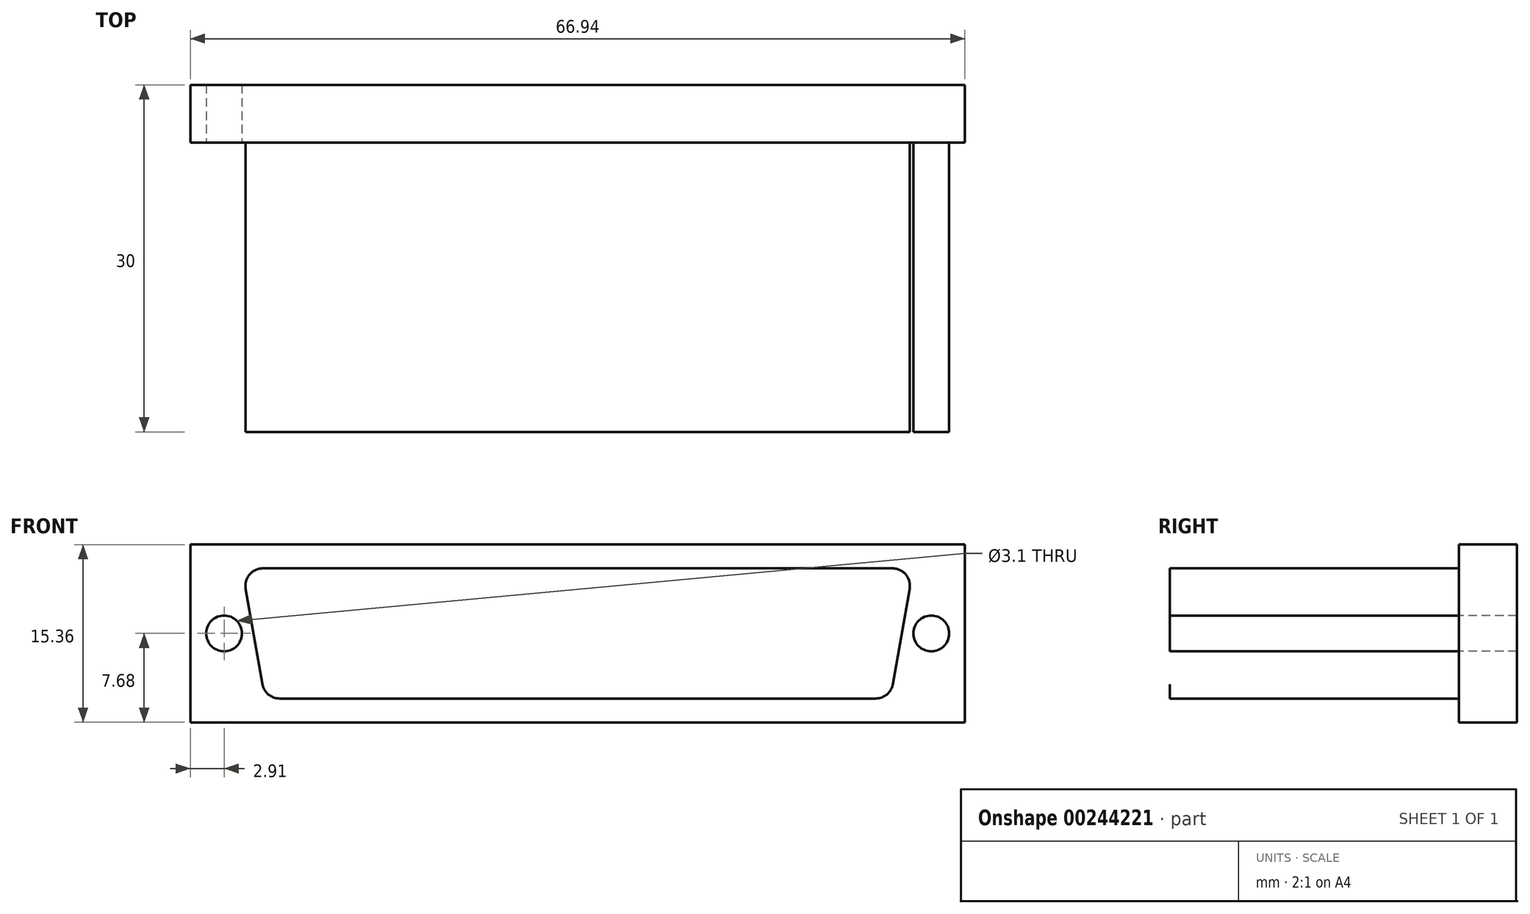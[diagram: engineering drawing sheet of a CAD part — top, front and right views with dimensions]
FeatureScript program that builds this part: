
annotation { "Feature Type Name" : "Feature", "Feature Type Description" : "" }
export const myFeature = defineFeature(function(context is Context, id is Id, definition is map)
    precondition{}
    {
        {
            var Q0;
            Q0=qCreatedBy(makeId("Front.planeOp"),FACE);
            var sketch = newSketch(context, id + "F0", { "sketchPlane" : qUnion([Q0])});
            skLineSegment(sketch, "E0.bottom", {"start": v(-33.47, 7.68) * mm, "end": v(33.47, 7.68) * mm});
            skLineSegment(sketch, "E0.top", {"start": v(-33.47, -7.68) * mm, "end": v(33.47, -7.68) * mm});
            skLineSegment(sketch, "E0.left", {"start": v(-33.47, 7.68) * mm, "end": v(-33.47, -7.68) * mm});
            skLineSegment(sketch, "E0.right", {"start": v(33.47, 7.68) * mm, "end": v(33.47, -7.68) * mm});
            skPoint(sketch, "E0.middle", {"position": v(0, 0) * mm});
            skCircle(sketch, "E1", {"center": v(30.56, 0) * mm, "radius": 1.55 * mm});
            skLineSegment(sketch, "E2", {"start": v(-33.47, 5.62) * mm, "end": v(33.47, 5.62) * mm, "construction": true});
            skLineSegment(sketch, "E3.MirrorCS", {"start": v(-33.47, -5.62) * mm, "end": v(33.47, -5.62) * mm, "construction": true});
            skCircle(sketch, "E4.MirrorC", {"center": v(-30.56, 0) * mm, "radius": 1.55 * mm});
            skLineSegment(sketch, "E5", {"start": v(28.69, 3.86) * mm, "end": v(27.23, -4.39) * mm});
            skLineSegment(sketch, "E6", {"start": v(29, 5.62) * mm, "end": v(29, -21.88) * mm, "construction": true});
            skLineSegment(sketch, "E7", {"start": v(0, 5.62) * mm, "end": v(27.21, 5.62) * mm});
            skLineSegment(sketch, "E8", {"start": v(0, -5.62) * mm, "end": v(25.76, -5.63) * mm});
            skPoint(sketch, "E9.visualSharp", {"position": v(29, 5.63) * mm});
            skArc(sketch, "E9.filletArc", {"start": v(28.69, 3.86) * mm, "mid": v(28.36, 5.09) * mm, "end": v(27.21, 5.62) * mm});
            skPoint(sketch, "E10.visualSharp", {"position": v(27.02, -5.63) * mm});
            skArc(sketch, "E10.filletArc", {"start": v(25.76, -5.63) * mm, "mid": v(26.72, -5.27) * mm, "end": v(27.23, -4.39) * mm});
            skLineSegment(sketch, "E11.MirrorCS", {"start": v(0, -5.62) * mm, "end": v(-25.76, -5.63) * mm});
            skLineSegment(sketch, "E12.MirrorCS", {"start": v(0, 5.62) * mm, "end": v(-27.21, 5.62) * mm});
            skLineSegment(sketch, "E13.MirrorCS", {"start": v(-28.69, 3.86) * mm, "end": v(-27.23, -4.39) * mm});
            skArc(sketch, "E14.MirrorCS", {"start": v(-28.69, 3.86) * mm, "mid": v(-28.36, 5.09) * mm, "end": v(-27.21, 5.62) * mm});
            skArc(sketch, "E15.MirrorCS", {"start": v(-25.76, -5.63) * mm, "mid": v(-26.72, -5.27) * mm, "end": v(-27.23, -4.39) * mm});
            skSolve(sketch);
        }
        {
            var Q0;
            Q0=makeQuery(id+"F0.imprint","IMPRINT",FACE,{"disambiguationData":[TD([[makeQuery(id+"F0.imprint","IMPRINT",EDGE,{"derivedFrom":sQuery(id+"F0.wireOp",EDGE,"E5")}),-1.0]])]});
            var Q1;
            Q1=makeQuery(id+"F0.imprint","IMPRINT",FACE,{"disambiguationData":[TD([[makeQuery(id+"F0.imprint","IMPRINT",EDGE,{"derivedFrom":sQuery(id+"F0.wireOp",EDGE,"E4.MirrorC")}),-1.0]])]});
            var Q2;
            Q2=makeQuery(id+"F0.imprint","IMPRINT",FACE,{"disambiguationData":[TD([[makeQuery(id+"F0.imprint","IMPRINT",EDGE,{"derivedFrom":sQuery(id+"F0.wireOp",EDGE,"E1")}),1.0]])]});
            extrude(context, id + "F1", {"entities" : qUnion([Q0, Q1, Q2]), "depth" : 25 * mm});
        }
        {
            var Q0;
            Q0=makeQuery(id+"F0.imprint","IMPRINT",FACE,{"disambiguationData":[TD([[makeQuery(id+"F0.imprint","IMPRINT",EDGE,{"derivedFrom":sQuery(id+"F0.wireOp",EDGE,"E0.bottom")}),-1.0]])]});
            var Q1;
            Q1=makeQuery(id+"F0.imprint","IMPRINT",FACE,{"disambiguationData":[TD([[makeQuery(id+"F0.imprint","IMPRINT",EDGE,{"derivedFrom":sQuery(id+"F0.wireOp",EDGE,"E5")}),-1.0]])]});
            var Q2;
            Q2=makeQuery(id+"F0.imprint","IMPRINT",FACE,{"disambiguationData":[TD([[makeQuery(id+"F0.imprint","IMPRINT",EDGE,{"derivedFrom":sQuery(id+"F0.wireOp",EDGE,"E1")}),1.0]])]});
            var Q3;
            Q3=makeQuery(id+"F0.imprint","IMPRINT",FACE,{"disambiguationData":[TD([[makeQuery(id+"F0.imprint","IMPRINT",EDGE,{"derivedFrom":sQuery(id+"F0.wireOp",EDGE,"E4.MirrorC")}),-1.0]])]});
            extrude(context, id + "F2", {"entities" : qUnion([Q0, Q1, Q2, Q3]), "operationType" : NewBodyOperationType.ADD, "oppositeDirection" : true, "depth" : 5 * mm});
        }
    });
